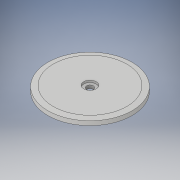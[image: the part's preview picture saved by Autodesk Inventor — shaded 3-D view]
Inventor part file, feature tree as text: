
AUTODESK INVENTOR PART (.ipt)
format: ipt  version: 2019 (Build 230136000, 136)  size: 131,584 bytes
history: native  units: mm
features: sketch x3, other x1, hole x1, extrude x1, chamfer x1, pattern_circular x1
ambient origin geometry x8: Origin, YZ Plane, XZ Plane, XY Plane, X Axis, Y Axis, Z Axis, Center Point
bodies: Solide1 (feature_tree)
feature tree (8):
  other  "Révolution1"
  hole  "Perçage1"  [1 undecoded]
  extrude  "Extrusion1"  Depth=4.0mm
  chamfer  "Chanfrein1"  Distance=5.0mm
  pattern_circular  "Réseau circulaire1"  Count=8  [1 undecoded]
  sketch  "Esquisse3"
  sketch  "Esquisse4"
  sketch  "Esquisse5"
note: 2 required parameter values undecoded (feature->parameter linkage not recoverable at this tier; creation-order binding heuristic only, values carry confidence <= 0.55)
